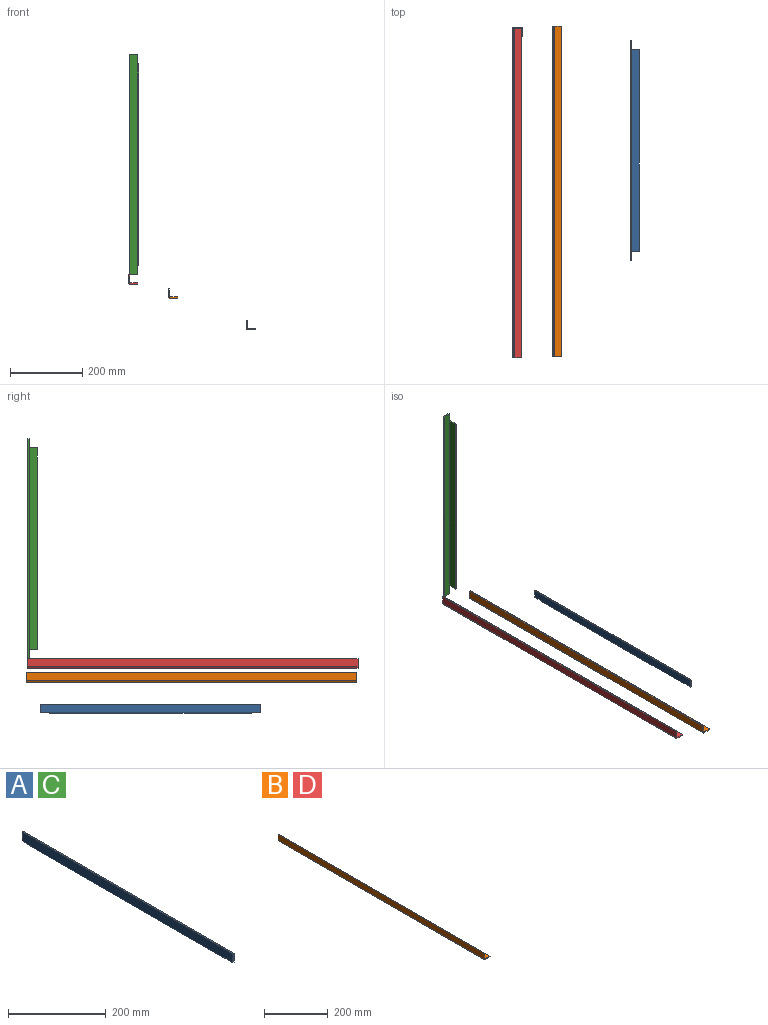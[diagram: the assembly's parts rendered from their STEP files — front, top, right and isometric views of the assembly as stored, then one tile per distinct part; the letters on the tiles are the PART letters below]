
ASSEMBLY  parts=4 mates=1
PART A: 13 faces, bbox 25.4x609.6x25.4 mm
  f0: plane 609.6x22.23mm, normal (-1,0,0), area 13548.3mm2, adj f1,f5,f7,f8,f9,f10,f11,f12
  f1: cylinder r=3.17mm len=558.8mm, axis (0,1,0), area 2786.9mm2, adj f0,f2,f9,f11
  f2: plane 558.8x22.23mm, normal (0,0,-1), area 12419.3mm2, adj f1,f3,f9,f11
  f3: plane 558.8x3.18mm, normal (1,0,0), area 1774.2mm2, adj f2,f4,f9,f11
  f4: plane 558.8x22.23mm, normal (0,0,1), area 12419.3mm2, adj f3,f6,f9,f11
  f5: plane 22.22x3.18mm, normal (0,1,0), area 70.6mm2, adj f0,f6,f7,f10
  f6: plane 609.6x22.23mm, normal (1,0,0), area 13548.3mm2, adj f4,f5,f7,f8,f10,f12
  f7: plane 609.6x3.18mm, normal (0,0,1), area 1935.5mm2, adj f0,f5,f6,f8
  f8: plane 22.22x3.18mm, normal (0,-1,0), area 70.6mm2, adj f0,f6,f7,f12
  f9: plane 25.4x3.18mm, normal (0,1,0), area 78.5mm2, adj f0,f1,f2,f3,f4,f10
  f10: plane 25.4x3.18mm, normal (0,0,-1), area 80.6mm2, adj f0,f5,f6,f9
  f11: plane 25.4x3.18mm, normal (0,-1,0), area 78.5mm2, adj f0,f1,f2,f3,f4,f12
  f12: plane 25.4x3.18mm, normal (0,0,-1), area 80.6mm2, adj f0,f6,f8,f11
PART B: 10 faces, bbox 25.4x914.4x25.4 mm
  f0: plane 914.4x22.23mm, normal (0,0,-1), area 20322.5mm2, adj f1,f7,f8,f9
  f1: plane 914.4x3.18mm, normal (1,0,0), area 2903.2mm2, adj f0,f2,f8,f9
  f2: plane 914.4x19.05mm, normal (0,0,1), area 17419.3mm2, adj f1,f3,f8,f9
  f3: cylinder r=3.17mm len=914.4mm, axis (0,1,0), area 4560.4mm2, adj f2,f4,f8,f9
  f4: plane 914.4x19.05mm, normal (1,0,0), area 17419.3mm2, adj f3,f5,f8,f9
  f5: plane 914.4x3.18mm, normal (0,0,1), area 2903.2mm2, adj f4,f6,f8,f9
  f6: plane 914.4x22.23mm, normal (-1,0,0), area 20322.5mm2, adj f5,f7,f8,f9
  f7: cylinder r=3.17mm len=914.4mm, axis (0,1,0), area 4560.4mm2, adj f0,f6,f8,f9
  f8: plane 25.4x25.4mm, normal (0,-1,0), area 151.2mm2, adj f0,f1,f2,f3,f4,f5,f6,f7
  f9: plane 25.4x25.4mm, normal (0,1,0), area 151.2mm2, adj f0,f1,f2,f3,f4,f5,f6,f7
PART C: same geometry as A
PART D: same geometry as B
PLACE A t=(93.98,23.12,-89.65)mm
PLACE B t=(-121.97,-89.58,-3.43)mm
PLACE C rot(axis=(0.58,-0.58,-0.58),120deg) t=(-203.75,362.46,365.59)mm
PLACE D t=(-232.33,-94.74,35.39)mm
MATE planar C.f8 <-> D.f5  axis (0,0,-1) through (-229.15,362.46,60.79)mm
